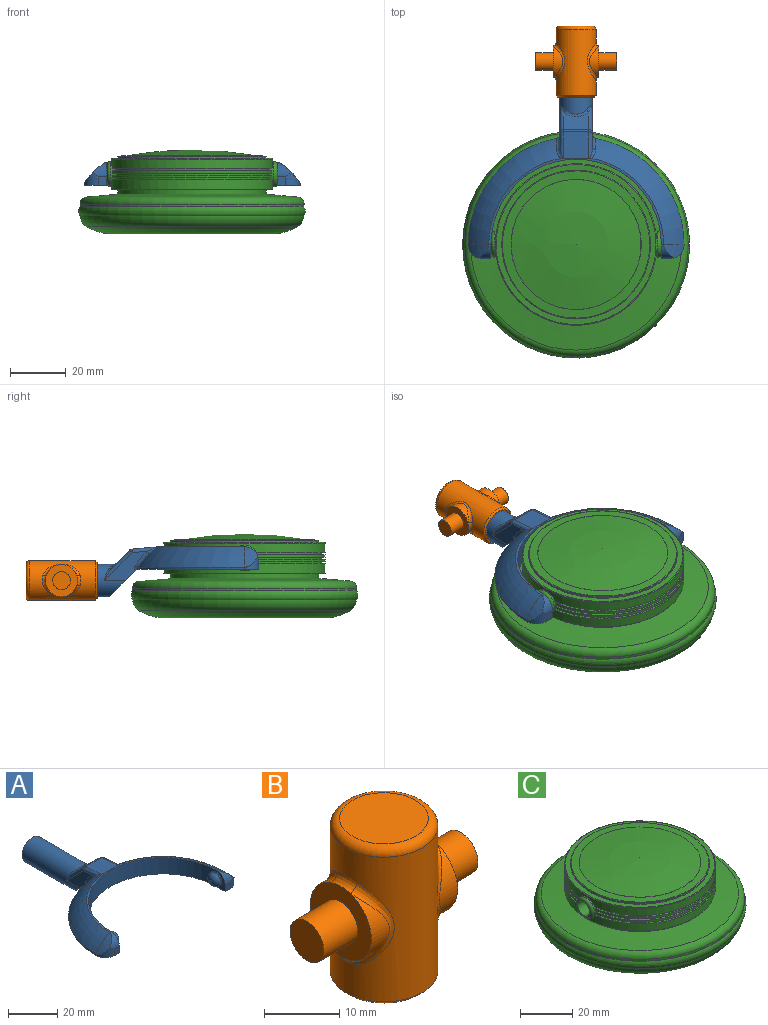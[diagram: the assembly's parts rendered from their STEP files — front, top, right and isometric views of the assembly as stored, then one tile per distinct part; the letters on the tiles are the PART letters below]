
ASSEMBLY  parts=3 mates=2
PART A: 48 faces, bbox 77.3x80.8x18.2 mm
  f0: plane 11.99x9.83mm, normal (0,-0.71,-0.71), area 141.5mm2, adj f1,f2,f9,f30,f43,f46
  f1: plane 15.39x10.49mm, normal (-1,0,0), area 63.5mm2, adj f0,f30,f32,f36,f46,f47
  f2: plane 15.39x10.49mm, normal (1,0,0), area 63.5mm2, adj f0,f30,f34,f39,f43,f44
  f3: plane 9.14x6.37mm, normal (0,0.71,0.71), area 67.6mm2, adj f35,f36,f39,f40
  f4: cylinder r=38.61mm len=37.99mm, axis (0,0,-1), area 42.6mm2, adj f6,f9,f17,f46,f47
  f5: torus R=19.3mm, axis (0,0,-1), area 507.8mm2, adj f10,f11,f12,f29,f42,f44
  f6: torus R=19.3mm, axis (0,0,-1), area 507.8mm2, adj f4,f11,f15,f28,f45,f47
  f7: cylinder r=30.48mm len=60.96mm, axis (0,0,-1), area 746.6mm2, adj f8,f9,f11,f14,f21,f24
  f8: plane 8.13x5.08mm, normal (-1,0,0), area 19.9mm2, adj f7,f9,f13,f19,f24
  f9: plane 77.22x43.73mm, normal (0,0,-1), area 956.2mm2, adj f0,f4,f7,f8,f10,f13,f14,f16
  f10: cylinder r=38.61mm len=37.99mm, axis (0,0,-1), area 42.6mm2, adj f5,f9,f20,f43,f44
  f11: plane 62.55x30.95mm, normal (0,0,1), area 75mm2, adj f5,f6,f7,f18,f19,f27
  f12: cylinder r=22.71mm len=7.33mm, axis (0,1,0), area 24.8mm2, adj f5,f19,f20
  f13: plane 3.05x3.05mm, normal (0,-1,0), area 9.3mm2, adj f8,f9,f19,f20
  f14: plane 8.13x5.08mm, normal (1,0,0), area 19.9mm2, adj f7,f9,f16,f18,f21
  f15: cylinder r=22.71mm len=7.33mm, axis (0,1,0), area 24.8mm2, adj f6,f17,f18
  f16: plane 3.05x3.05mm, normal (0,-1,0), area 9.3mm2, adj f9,f14,f17,f18
  f17: cylinder r=5.08mm len=5.08mm, axis (0,0,-1), area 21.9mm2, adj f4,f9,f15,f16,f18
  f18: cylinder r=5.08mm len=5.08mm, axis (-1,0,0), area 21.9mm2, adj f11,f14,f15,f16,f17
  f19: cylinder r=5.08mm len=5.08mm, axis (-1,0,0), area 21.9mm2, adj f8,f11,f12,f13,f20
  f20: cylinder r=5.08mm len=5.08mm, axis (0,0,-1), area 21.9mm2, adj f9,f10,f12,f13,f19
  f21: cylinder r=3.17mm len=6.35mm, axis (-1,0,0), area 12.7mm2, adj f7,f14,f23
  f22: plane 1.27x1.27mm, normal (1,0,0), area 1.3mm2, adj f23
  f23: torus R=0.64mm, axis (1,0,0), area 56.5mm2, adj f21,f22
  f24: cylinder r=3.17mm len=6.35mm, axis (1,0,0), area 12.7mm2, adj f7,f8,f26
  f25: plane 1.27x1.27mm, normal (-1,0,0), area 1.3mm2, adj f26
  f26: torus R=0.64mm, axis (-1,0,0), area 56.5mm2, adj f24,f25
  f27: plane 9.86x9.36mm, normal (0,0.09,1), area 85.6mm2, adj f11,f28,f29,f32,f34,f35,f42,f45
  f28: plane 1.04x0.17mm, normal (0,-1,0), area 0mm2, adj f6,f27,f45
  f29: plane 1.04x0.17mm, normal (0,-1,0), area 0mm2, adj f5,f27,f42
  f30: cylinder r=5.84mm len=33.01mm, axis (0,-1,0), area 1029.7mm2, adj f0,f1,f2,f31,f38,f40,f41
  f31: plane 11.68x11.68mm, normal (0,1,0), area 107.2mm2, adj f30
  f32: cylinder r=1.27mm len=9.13mm, axis (0,-1,0.09), area 14.4mm2, adj f1,f27,f33,f45
  f33: sphere r=1.27mm, area 1.5mm2, adj f32,f35,f36
  f34: cylinder r=1.27mm len=9.13mm, axis (0,1,-0.09), area 14.4mm2, adj f2,f27,f37,f42
  f35: cylinder r=1.27mm len=9.14mm, axis (-1,0,0), area 8.1mm2, adj f3,f27,f33,f37
  f36: cylinder r=1.27mm len=10.91mm, axis (0,-0.71,0.71), area 23.1mm2, adj f1,f3,f33,f38
  f37: sphere r=1.27mm, area 1.5mm2, adj f34,f35,f39
  f38: bspline ~4.55x2.75mm, area 2.3mm2, adj f30,f36,f40
  f39: cylinder r=1.27mm len=10.91mm, axis (0,0.71,-0.71), area 23.1mm2, adj f2,f3,f37,f41
  f40: bspline ~9.14x2.56mm, area 10.7mm2, adj f3,f30,f38,f41
  f41: bspline ~5.23x3.53mm, area 2.3mm2, adj f30,f39,f40
  f42: bspline ~4.62x3.14mm, area 5.2mm2, adj f5,f27,f29,f34,f44
  f43: cylinder r=1.27mm len=1.74mm, axis (0,0,-1), area 1.9mm2, adj f0,f2,f9,f10,f44
  f44: bspline ~8.6x7.86mm, area 11.9mm2, adj f2,f5,f10,f42,f43
  f45: bspline ~4.62x3.14mm, area 5.2mm2, adj f6,f27,f28,f32,f47
  f46: cylinder r=1.27mm len=1.74mm, axis (0,0,-1), area 1.9mm2, adj f0,f1,f4,f9,f47
  f47: bspline ~8.6x7.86mm, area 11.9mm2, adj f1,f4,f6,f45,f46
PART B: 25 faces, bbox 28.9x15.5x25.4 mm
  f0: cylinder r=5.71mm len=10.81mm, axis (-1,0,0), area 26.2mm2, adj f5,f15
  f1: cylinder r=5.71mm len=10.81mm, axis (-1,0,0), area 26.2mm2, adj f8,f11
  f2: cylinder r=7.14mm len=23.5mm, axis (0,0,-1), area 763.2mm2, adj f9,f10,f11,f12,f13,f14,f15,f16
  f3: plane 11.75x11.75mm, normal (0,0,1), area 108.4mm2, adj f17
  f4: plane 13.02x13.02mm, normal (0,0,-1), area 16.3mm2, adj f22,f24
  f5: plane 11.46x11.46mm, normal (1,0,0), area 70.9mm2, adj f0,f6,f13,f16,f18
  f6: cylinder r=5.71mm len=10.81mm, axis (-1,0,0), area 26.2mm2, adj f5,f14
  f7: cylinder r=5.71mm len=10.81mm, axis (-1,0,0), area 26.2mm2, adj f8,f10
  f8: plane 11.46x11.46mm, normal (-1,0,0), area 70.9mm2, adj f1,f7,f9,f12,f20
  f9: bspline ~4.64x1.73mm, area 6.5mm2, adj f2,f8,f10,f11
  f10: bspline ~13.62x4.91mm, area 20.7mm2, adj f2,f7,f9,f12
  f11: bspline ~13.6x4.87mm, area 20.7mm2, adj f1,f2,f9,f12
  f12: bspline ~4.64x1.73mm, area 6.5mm2, adj f2,f8,f10,f11
  f13: bspline ~4.64x1.73mm, area 6.5mm2, adj f2,f5,f14,f15
  f14: bspline ~13.62x4.91mm, area 20.7mm2, adj f2,f6,f13,f16
  f15: bspline ~13.6x4.87mm, area 20.7mm2, adj f0,f2,f13,f16
  f16: bspline ~4.64x1.73mm, area 6.5mm2, adj f2,f5,f14,f15
  f17: torus R=5.87mm, axis (0,0,1), area 83.8mm2, adj f2,f3
  f18: cylinder r=3.17mm len=6.35mm, axis (-1,0,0), area 126.7mm2, adj f5,f19
  f19: plane 6.35x6.35mm, normal (1,0,0), area 31.7mm2, adj f18
  f20: cylinder r=3.17mm len=6.35mm, axis (1,0,0), area 126.7mm2, adj f8,f21
  f21: plane 6.35x6.35mm, normal (-1,0,0), area 31.7mm2, adj f20
  f22: cylinder r=6.1mm len=22.86mm, axis (0,0,-1), area 875.6mm2, adj f4,f23
  f23: plane 12.19x12.19mm, normal (0,0,-1), area 116.7mm2, adj f22
  f24: cone r=7.14mm half-angle=45deg, axis (0,0,1), area 38.5mm2, adj f2,f4
PART C: 49 faces, bbox 88.9x88.9x30 mm
  f0: cylinder r=28.87mm len=57.73mm, axis (0,0,-1), area 595.8mm2, adj f3,f4,f39,f40,f45
  f1: plane 57.06x24.48mm, normal (0,0,-1), area 101.4mm2, adj f6,f8,f39,f40
  f2: plane 57.06x24.48mm, normal (0,0,-1), area 101.4mm2, adj f5,f7,f39,f40
  f3: plane 57.13x24.71mm, normal (0,0,1), area 102mm2, adj f0,f6,f39,f40
  f4: plane 57.13x24.71mm, normal (0,0,1), area 102mm2, adj f0,f5,f39,f40
  f5: cylinder r=27.6mm len=54.56mm, axis (0,0,-1), area 49.6mm2, adj f2,f4,f39,f40
  f6: cylinder r=27.6mm len=54.56mm, axis (0,0,-1), area 49.6mm2, adj f1,f3,f39,f40
  f7: cylinder r=28.87mm len=57.06mm, axis (0,0,-1), area 77.8mm2, adj f2,f10,f39,f40
  f8: cylinder r=28.87mm len=57.06mm, axis (0,0,-1), area 77.8mm2, adj f1,f9,f39,f40
  f9: plane 57.01x24.31mm, normal (0,0,1), area 101mm2, adj f8,f12,f39,f40
  f10: plane 57.01x24.31mm, normal (0,0,1), area 101mm2, adj f7,f11,f39,f40
  f11: cylinder r=27.6mm len=54.44mm, axis (0,0,-1), area 49.2mm2, adj f10,f14,f39,f40
  f12: cylinder r=27.6mm len=54.44mm, axis (0,0,-1), area 49.2mm2, adj f9,f13,f39,f40
  f13: plane 57.01x24.31mm, normal (0,0,-1), area 101mm2, adj f12,f16,f39,f40
  f14: plane 57.01x24.31mm, normal (0,0,-1), area 101mm2, adj f11,f15,f39,f40
  f15: cylinder r=28.87mm len=57.06mm, axis (0,0,-1), area 77.8mm2, adj f14,f20,f39,f40
  f16: cylinder r=28.87mm len=57.06mm, axis (0,0,-1), area 77.8mm2, adj f13,f19,f39,f40
  f17: plane 57.13x24.71mm, normal (0,0,-1), area 102mm2, adj f22,f23,f39,f40
  f18: plane 57.13x24.71mm, normal (0,0,-1), area 102mm2, adj f21,f23,f39,f40
  f19: plane 57.06x24.48mm, normal (0,0,1), area 101.4mm2, adj f16,f22,f39,f40
  f20: plane 57.06x24.48mm, normal (0,0,1), area 101.4mm2, adj f15,f21,f39,f40
  f21: cylinder r=27.6mm len=54.56mm, axis (0,0,-1), area 49.6mm2, adj f18,f20,f39,f40
  f22: cylinder r=27.6mm len=54.56mm, axis (0,0,-1), area 49.6mm2, adj f17,f19,f39,f40
  f23: cylinder r=28.87mm len=57.73mm, axis (0,0,-1), area 595.8mm2, adj f17,f18,f39,f40,f46
  f24: plane 41.31x41.31mm, normal (0,0,-1), area 1340.4mm2, adj f25
  f25: torus R=22.66mm, axis (0,0,-1), area 989.6mm2, adj f24,f26
  f26: torus R=28.4mm, axis (0,0,-1), area 3558.3mm2, adj f25,f27
  f27: torus R=35.36mm, axis (0,0,-1), area 1114.4mm2, adj f26,f28
  f28: torus R=37.55mm, axis (0,0,-1), area 918.9mm2, adj f27,f29
  f29: cylinder r=40.07mm len=80.14mm, axis (0,0,-1), area 213.4mm2, adj f28,f33
  f30: cone r=26.58mm half-angle=85deg, axis (0,0,-1), area 2265.9mm2, adj f31,f33
  f31: cylinder r=26.58mm len=53.16mm, axis (0,0,-1), area 265.1mm2, adj f30,f32
  f32: plane 57.23x57.23mm, normal (0,0,-1), area 352.3mm2, adj f31,f45
  f33: torus R=37.53mm, axis (0,0,1), area 928.9mm2, adj f29,f30
  f34: sphere r=135.39mm, area 1711.1mm2, adj f48
  f35: cone r=26.58mm half-angle=87deg, axis (0,0,-1), area 477.5mm2, adj f47,f48
  f36: cylinder r=26.58mm len=53.16mm, axis (0,0,-1), area 92.3mm2, adj f37,f47
  f37: plane 57.23x57.23mm, normal (0,0,1), area 352.3mm2, adj f36,f46
  f38: plane 6.6x6.6mm, normal (1,0,0), area 2.6mm2, adj f43,f44
  f39: cylinder r=4.57mm len=9.14mm, axis (-1,0,0), area 20.2mm2, adj f0,f1,f2,f3,f4,f5,f6,f7
  f40: cylinder r=4.57mm len=9.14mm, axis (-1,0,0), area 20.2mm2, adj f0,f1,f2,f3,f4,f5,f6,f7
  f41: plane 6.6x6.6mm, normal (-1,0,0), area 2.6mm2, adj f42,f44
  f42: torus R=3.3mm, axis (1,0,0), area 51.5mm2, adj f40,f41
  f43: torus R=3.3mm, axis (1,0,0), area 51.5mm2, adj f38,f39
  f44: cylinder r=3.17mm len=60.96mm, axis (1,0,0), area 1216.1mm2, adj f38,f41
  f45: torus R=28.61mm, axis (0,0,1), area 72.1mm2, adj f0,f32
  f46: torus R=28.61mm, axis (0,0,-1), area 72.1mm2, adj f23,f37
  f47: torus R=26.33mm, axis (0,0,1), area 64.2mm2, adj f35,f36
  f48: torus R=23.29mm, axis (0,0,1), area 4.5mm2, adj f34,f35
PLACE A t=(32.34,27.52,20.85)mm
PLACE B rot(axis=(-1,0,0),90deg) t=(32.34,80.3,16.88)mm
PLACE C t=(32.34,27.52,33.52)mm
MATE revolute A.f24 <-> C.f39  axis (-1,0,0) through (62.82,27.52,24.92)mm
MATE revolute B.f2 <-> A.f30  axis (0,-1,0) through (32.34,103.16,16.88)mm
